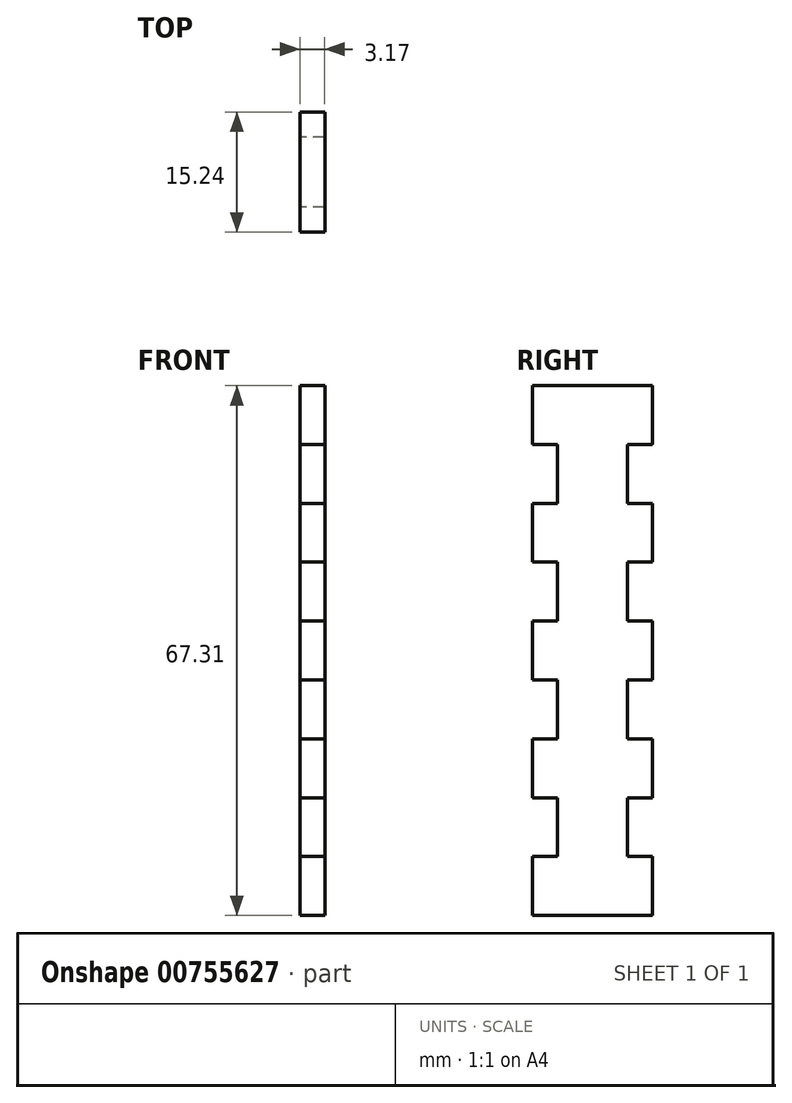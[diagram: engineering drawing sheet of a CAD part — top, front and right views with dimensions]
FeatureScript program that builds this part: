
annotation { "Feature Type Name" : "Feature", "Feature Type Description" : "" }
export const myFeature = defineFeature(function(context is Context, id is Id, definition is map)
    precondition{}
    {
        {
            var Q0;
            Q0=qCreatedBy(makeId("Right.planeOp"),FACE);
            var sketch = newSketch(context, id + "F0", { "sketchPlane" : qUnion([Q0])});
            skLineSegment(sketch, "E0.bottom", {"start": v(-86.36, 59.83) * mm, "end": v(-71.12, 59.83) * mm});
            skLineSegment(sketch, "E0.top", {"start": v(-86.36, -7.48) * mm, "end": v(-71.12, -7.48) * mm});
            skLineSegment(sketch, "E0.left", {"start": v(-86.36, 59.83) * mm, "end": v(-86.36, 52.35) * mm});
            skLineSegment(sketch, "E0.right", {"start": v(-71.12, 59.83) * mm, "end": v(-71.12, 52.35) * mm});
            skLineSegment(sketch, "E1", {"start": v(-83.19, 52.35) * mm, "end": v(-83.19, 44.87) * mm});
            skLineSegment(sketch, "E2", {"start": v(-86.36, 52.35) * mm, "end": v(-83.19, 52.35) * mm});
            skLineSegment(sketch, "E3", {"start": v(-86.36, 44.87) * mm, "end": v(-83.19, 44.87) * mm});
            skLineSegment(sketch, "E4", {"start": v(-86.36, 37.4) * mm, "end": v(-83.19, 37.4) * mm});
            skLineSegment(sketch, "E5", {"start": v(-86.87, 29.92) * mm, "end": v(-83.19, 29.92) * mm});
            skLineSegment(sketch, "E6", {"start": v(-86.36, 22.44) * mm, "end": v(-83.19, 22.44) * mm});
            skLineSegment(sketch, "E7", {"start": v(-86.36, 14.96) * mm, "end": v(-83.19, 14.96) * mm});
            skLineSegment(sketch, "E8", {"start": v(-86.36, 7.48) * mm, "end": v(-83.19, 7.48) * mm});
            skLineSegment(sketch, "E9", {"start": v(-86.36, 0) * mm, "end": v(-83.19, 0) * mm});
            skLineSegment(sketch, "E10.MirrorCS", {"start": v(-74.3, 52.35) * mm, "end": v(-74.3, 44.87) * mm});
            skLineSegment(sketch, "E11", {"start": v(-74.3, 52.35) * mm, "end": v(-71.12, 52.35) * mm});
            skLineSegment(sketch, "E12", {"start": v(-74.3, 44.87) * mm, "end": v(-71.12, 44.87) * mm});
            skLineSegment(sketch, "E13", {"start": v(-74.3, 37.4) * mm, "end": v(-71.12, 37.4) * mm});
            skLineSegment(sketch, "E14", {"start": v(-74.3, 29.92) * mm, "end": v(-71.12, 29.92) * mm});
            skLineSegment(sketch, "E15", {"start": v(-74.3, 22.44) * mm, "end": v(-71.12, 22.44) * mm});
            skLineSegment(sketch, "E16", {"start": v(-74.3, 14.96) * mm, "end": v(-71.12, 14.96) * mm});
            skLineSegment(sketch, "E17", {"start": v(-74.3, 7.48) * mm, "end": v(-71.12, 7.48) * mm});
            skLineSegment(sketch, "E18", {"start": v(-74.3, 0) * mm, "end": v(-71.12, 0) * mm});
            skLineSegment(sketch, "E19.trimOffspring", {"start": v(-86.36, 44.87) * mm, "end": v(-86.36, 37.4) * mm});
            skLineSegment(sketch, "E20.trimOffspring", {"start": v(-86.36, 29.92) * mm, "end": v(-86.36, 22.44) * mm});
            skLineSegment(sketch, "E21.trimOffspring", {"start": v(-86.36, 14.96) * mm, "end": v(-86.36, 7.48) * mm});
            skLineSegment(sketch, "E22.trimOffspring", {"start": v(-86.36, 0) * mm, "end": v(-86.36, -7.48) * mm});
            skLineSegment(sketch, "E23.trimOffspring", {"start": v(-71.12, 0) * mm, "end": v(-71.12, -7.48) * mm});
            skLineSegment(sketch, "E24.trimOffspring", {"start": v(-71.12, 14.96) * mm, "end": v(-71.12, 7.48) * mm});
            skLineSegment(sketch, "E25.trimOffspring", {"start": v(-71.12, 29.92) * mm, "end": v(-71.12, 22.44) * mm});
            skLineSegment(sketch, "E26.trimOffspring", {"start": v(-71.12, 44.87) * mm, "end": v(-71.12, 37.4) * mm});
            skPoint(sketch, "E27.orphan", {"position": v(-83.19, 59.83) * mm});
            skPoint(sketch, "E28.end.orphan", {"position": v(-78.74, -7.48) * mm});
            skPoint(sketch, "E28.start.orphan", {"position": v(-78.74, 59.83) * mm});
            skLineSegment(sketch, "E29.trimOffspring", {"start": v(-74.3, 37.4) * mm, "end": v(-74.3, 29.92) * mm});
            skLineSegment(sketch, "E30.trimOffspring", {"start": v(-74.3, 22.44) * mm, "end": v(-74.3, 14.96) * mm});
            skLineSegment(sketch, "E31.trimOffspring", {"start": v(-74.3, 7.48) * mm, "end": v(-74.3, 0) * mm});
            skPoint(sketch, "E32.orphan", {"position": v(-83.19, -7.48) * mm});
            skLineSegment(sketch, "E33.trimOffspring", {"start": v(-83.19, 7.48) * mm, "end": v(-83.19, 0) * mm});
            skLineSegment(sketch, "E34.trimOffspring", {"start": v(-83.19, 22.44) * mm, "end": v(-83.19, 14.96) * mm});
            skLineSegment(sketch, "E35.trimOffspring", {"start": v(-83.19, 37.4) * mm, "end": v(-83.19, 29.92) * mm});
            skSolve(sketch);
        }
        {
            var Q0;
            Q0=makeQuery(id+"F0.imprint","IMPRINT",FACE,{"disambiguationData":[TD([[makeQuery(id+"F0.imprint","IMPRINT",EDGE,{"derivedFrom":sQuery(id+"F0.wireOp",EDGE,"E0.bottom")}),-1.0]])]});
            extrude(context, id + "F1", {"entities" : qUnion([Q0]), "depth" : 3.17 * mm, "offsetDistance" : 25.4 * mm});
        }
    });
